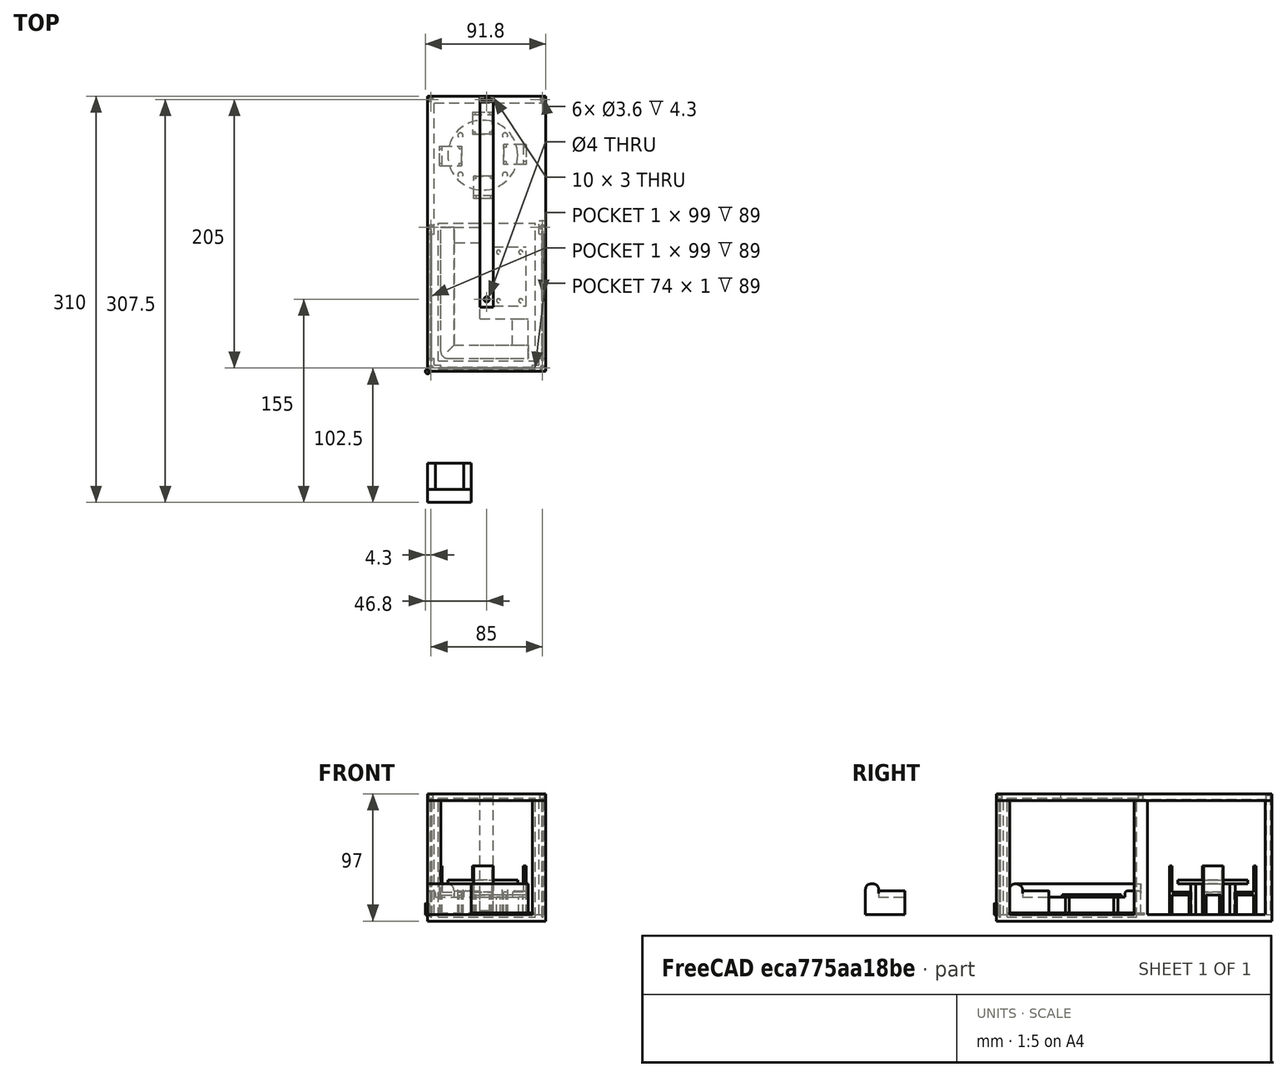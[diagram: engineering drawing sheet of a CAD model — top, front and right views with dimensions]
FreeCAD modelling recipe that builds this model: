
FCSTD DOCUMENT  (FreeCAD 0.15R4671 (Git))
Label: Salon
License: CreativeCommons Attribution-ShareAlike
LicenseURL: http://creativecommons.org/licenses/by-sa/4.0/
objects: Part::Box×28, Part::Feature×14, Part::MultiFuse×12, Part::Cut×5, Part::Cylinder×4, Part::FeaturePython×3, App::DocumentObjectGroup×2, Part::Fillet×2, Part::Offset×1
note: 69 computed .brp shape members not serialized (recipe doc carries the construction recipe); baked Part::Feature solids carry a one-line shape summary decoded from their .brp

FEATURE [Part::Box] Box  label="suelo macizo conteiner 20""
  Height = 5
  Length = 90
  Placement = pos=(0,0,-5) rot=(0,0,1;0rad)
  Width = 210
FEATURE [Part::Box] Box001  label="Techo macizo conteiner 20""
  Height = 5
  Length = 90
  Placement = pos=(0,0,87) rot=(0,0,1;0rad)
  Width = 210
FEATURE [Part::Box] Box002  label="larguero vertical esquina 1_1"
  Height = 87
  Length = 10
  Width = 5
FEATURE [Part::Box] Box003  label="larguero vertical esquina 1_2"
  Height = 87
  Length = 5
  Width = 10
FEATURE [Part::MultiFuse] Fusion  label="Larguero esquina 1 Salon"
  Shapes = -> [Box002,Box003]
FEATURE [Part::Box] Box004  label="larguero vertical esquina 2_1"
  Height = 87
  Length = 10
  Placement = pos=(80,0,0) rot=(0,0,1;0rad)
  Width = 5
FEATURE [Part::Box] Box005  label="larguero vertical esquina 2_2"
  Height = 87
  Length = 5
  Placement = pos=(85,0,0) rot=(0,0,1;0rad)
  Width = 10
FEATURE [Part::MultiFuse] Fusion001  label="Larguero esquina 2 Salon"
  Shapes = -> [Box004,Box005]
FEATURE [Part::Box] Box007  label="Tabique macizo trasero salon"
  Height = 87
  Length = 5
  Placement = pos=(85,205,0) rot=(0,0,1;0rad)
  Width = 5
FEATURE [Part::Box] Box008  label="Tabique macizo lateral salon"
  Height = 87
  Length = 80
  Placement = pos=(5,205,0) rot=(0,0,1;0rad)
  Width = 5
FEATURE [Part::Box] Box009  label="Esquina maciza linde derecha con modulo entrada"
  Height = 87
  Length = 5
  Placement = pos=(0,105,0) rot=(0,0,1;0rad)
  Width = 105
FEATURE [Part::MultiFuse] Fusion002  label="Pared Esquinazo Salon"
  Shapes = -> [Box007,Box008,Box009]
FEATURE [Part::Cylinder] Cylinder002  label="conector master"
  Angle = 360
  Height = 8
  Radius = 1.5
FEATURE [Part::Offset] Offset  label="Offset conector master"
  Fill = false
  Intersection = false
  Join = 2
  Mode = 1
  SelfIntersection = false
  Source = -> Cylinder002
  Value = 0.3
FEATURE [Part::Feature] Offset001001  label="Vaciado conector 1"
  Placement = pos=(2.5,2.5,83) rot=(0,0,1;0rad)
  shape: bbox 3.602 x 3.602 x 8.602 mm, 3 faces (baked)
FEATURE [Part::Feature] Offset002001  label="Vaciado conector 2"
  Placement = pos=(87.5,2.5,83) rot=(0,0,1;0rad)
  shape: bbox 3.602 x 3.602 x 8.602 mm, 3 faces (baked)
FEATURE [Part::Feature] Offset002002002001  label="Vaciado conector 3"
  Placement = pos=(87.5,110,83) rot=(0,0,1;0rad)
  shape: bbox 3.602 x 3.602 x 8.602 mm, 3 faces (baked)
FEATURE [Part::Feature] Offset002002002002001  label="Vaciado conector 4"
  Placement = pos=(87.5,207.5,83) rot=(0,0,1;0rad)
  shape: bbox 3.602 x 3.602 x 8.602 mm, 3 faces (baked)
FEATURE [Part::Feature] Offset001002  label="Vaciado conector 5"
  Placement = pos=(2.5,207.5,83) rot=(0,0,1;0rad)
  shape: bbox 3.602 x 3.602 x 8.602 mm, 3 faces (baked)
FEATURE [Part::Feature] Offset001002002001  label="Vaciado conector 6"
  Placement = pos=(2.5,110,83) rot=(0,0,1;0rad)
  shape: bbox 3.602 x 3.602 x 8.602 mm, 3 faces (baked)
FEATURE [Part::Box] Box020  label="cristal salon lateral"
  Height = 91
  Length = 74
  Placement = pos=(8,2,-2) rot=(0,0,1;0rad)
  Width = 1
FEATURE [Part::Box] Box021002  label="cristal salon trasero"
  Height = 91
  Length = 1
  Placement = pos=(2,8,-2) rot=(0,0,1;0rad)
  Width = 99
FEATURE [Part::Feature] Cylinder003001  label="Hueco Techo Led Salon"
  Placement = pos=(45,55,81) rot=(0,0,1;0rad)
  shape: bbox 4 x 4 x 10 mm, 3 faces (baked)
FEATURE [Part::Box] Box021003006  label="Cristal salon frontal"
  Height = 91
  Length = 1
  Placement = pos=(87,8,-2) rot=(0,0,1;0rad)
  Width = 99
FEATURE [Part::Box] Box021003007  label="Tabique izquierdo union con modulo entrada "
  Height = 87
  Length = 5
  Placement = pos=(85,105,0) rot=(0,0,1;0rad)
  Width = 10
FEATURE [Part::Feature] Cylinder002001  label="conector 1"
  Placement = pos=(2.5,2.5,83) rot=(0,0,1;0rad)
  shape: bbox 3 x 3 x 8 mm, 3 faces (baked)
FEATURE [Part::Feature] Cylinder002001001  label="conector 2"
  Placement = pos=(87.5,2.5,83) rot=(0,0,1;0rad)
  shape: bbox 3 x 3 x 8 mm, 3 faces (baked)
FEATURE [Part::Feature] Cylinder002001002  label="conector 3"
  Placement = pos=(87.5,110,83) rot=(0,0,1;0rad)
  shape: bbox 3 x 3 x 8 mm, 3 faces (baked)
FEATURE [Part::Feature] Cylinder002001003  label="conector 4"
  Placement = pos=(87.5,207.5,83) rot=(0,0,1;0rad)
  shape: bbox 3 x 3 x 8 mm, 3 faces (baked)
FEATURE [Part::Feature] Cylinder002001004  label="conector 5"
  Placement = pos=(2.5,207.5,83) rot=(0,0,1;0rad)
  shape: bbox 3 x 3 x 8 mm, 3 faces (baked)
FEATURE [Part::Feature] Cylinder002001005  label="conector 6"
  Placement = pos=(2.5,110,83) rot=(0,0,1;0rad)
  shape: bbox 3 x 3 x 8 mm, 3 faces (baked)
FEATURE [Part::MultiFuse] Fusion003  label="Union conectores"
  Shapes = -> [Cylinder002001,Cylinder002001001,Cylinder002001002,Cylinder002001003,Cylinder002001004,Cylinder002001005]
FEATURE [Part::MultiFuse] Fusion004  label="Union vaciados"
  Shapes = -> [Offset001001,Offset002001,Offset002002002001,Offset002002002002001,Offset001002,Offset001002002001]
FEATURE [Part::MultiFuse] Fusion005  label="Union suelo +paredes+conectores Salon"
  Shapes = -> [Box,Fusion,Fusion001,Box021003007,Fusion002,Fusion003]
FEATURE [Part::MultiFuse] Fusion006  label="Union cristales salon"
  Shapes = -> [Box020,Box021002,Box021003006]
FEATURE [Part::Cut] Cut  label="Suelo+Paredes Salon"
  Base = -> Fusion005
  Tool = -> Fusion006
FEATURE [Part::Cut] Cut001  label="Techo salon - vaciados conectores"
  Base = -> Box001
  Tool = -> Fusion004
FEATURE [Part::Box] Box021003008  label="Roza techo horizontal"
  Height = 5
  Length = 10
  Placement = pos=(40,49,88) rot=(0,0,1;0rad)
  Width = 160
FEATURE [Part::Box] Box021003009  label="Roza vertical"
  Height = 93
  Length = 10
  Placement = pos=(40,206,0) rot=(0,0,1;0rad)
  Width = 3
FEATURE [Part::Box] Box021003010  label="Salida cables roza hacia caja electronica"
  Height = 3
  Length = 10
  Placement = pos=(40,206,0) rot=(0,0,1;0rad)
  Width = 10
FEATURE [Part::MultiFuse] Fusion007  label="Roza led salon"
  Shapes = -> [Cylinder003001,Box021003008,Box021003009,Box021003010]
FEATURE [Part::Cut] Cut002  label="Suelo+Paredes Salon001"
  Base = -> Cut
  Tool = -> Fusion007
FEATURE [Part::Cut] Cut003  label="Techo - roza cable led"
  Base = -> Cut001
  Tool = -> Fusion007
FEATURE [Part::Cut] Cut004  label="Techo salon"
  Base = -> Cut003
  Tool = -> Fusion006
FEATURE [App::DocumentObjectGroup] Grupo001  label="Elementos constructivos Salon"
  Group = -> [Offset,Cut002,Cut004]
FEATURE [Part::Box] Box021003011  label="alfombra salon"
  Height = 1.2
  Length = 74
  Placement = pos=(8,8,0) rot=(0,0,1;0rad)
  Width = 105
FEATURE [Part::Box] Box021003013  label="respaldo izquierda"
  Height = 23.3333
  Length = 66.6667
  Width = 10
FEATURE [Part::Box] Box021003014  label="respaldo derecha"
  Height = 23.3333
  Length = 10
  Width = 100
FEATURE [Part::Box] Box021003015  label="asiento derecha"
  Height = 13.3333
  Length = 30
  Width = 100
FEATURE [Part::Box] Box021003016  label="Asiento izquierda"
  Height = 13.3333
  Length = 66.6667
  Width = 30
FEATURE [Part::Box] Box021003017  label="reposabrazos derecho"
  Height = 18
  Length = 30
  Placement = pos=(0,88,0) rot=(0,0,1;0rad)
  Width = 12
FEATURE [Part::Box] Box021003018  label="reposabrazos izquierdo"
  Height = 18
  Length = 12
  Placement = pos=(54.6667,0,0) rot=(0,0,1;0rad)
  Width = 30
FEATURE [Part::MultiFuse] Fusion008  label="Sofa salon"
  Placement = pos=(10,10,0) rot=(0,0,1;0rad)
  Shapes = -> [Box021003013,Box021003014,Box021003015,Box021003016,Box021003017,Box021003018]
FEATURE [Part::Fillet] Fillet  label="Sofa"
  Base = -> Fusion008
  Edges = 12 edges: [Edge5 r=5,Edge8 r=2,Edge12 r=2,Edge13 r=5,Edge19 r=2,Edge21 r=2,Edge25 r=4,Edge26 r=4,Edge27 r=4,Edge28 r=4,Edge37 r=5,Edge38 r=5]
FEATURE [Part::Box] Box021003019  label="tablero mesa sofa"
  Height = 2
  Length = 25
  Placement = pos=(50,50,13.3333) rot=(0,0,1;0rad)
  Width = 45
FEATURE [Part::Cylinder] Cylinder  label="pata mesa master"
  Angle = 360
  Height = 13.3333
  Placement = pos=(54,54,0) rot=(0,0,1;0rad)
  Radius = 1.5
FEATURE [Part::FeaturePython] Array  label="matriz 4 patas mesa sofa"  # Draft array (typed FeaturePython)
  Angle = 360
  ArrayType = 0
  Axis = (0,0,1)
  Base = -> Cylinder
  Center = (0,0,0)
  Fuse = false
  IntervalAxis = (0,0,0)
  IntervalX = (17,0,0)
  IntervalY = (0,37,0)
  IntervalZ = (0,0,0)
  NumberPolar = 1
  NumberX = 2
  NumberY = 2
  NumberZ = 1
FEATURE [Part::MultiFuse] Fusion009  label="mesa sofa"
  Shapes = -> [Box021003019,Array]
FEATURE [Part::Cylinder] Cylinder002001006  label="tablero mesa comedor"
  Angle = 360
  Height = 3
  Placement = pos=(42,165,23.3333) rot=(0,0,1;0rad)
  Radius = 26.6667
FEATURE [Part::Cylinder] Cylinder002001007  label="pata master mesa comedor"
  Angle = 360
  Height = 23.3333
  Placement = pos=(25,150,0) rot=(0,0,1;0rad)
  Radius = 2
FEATURE [Part::FeaturePython] Array001  label="matriz 4 patas mesa comedor"  # Draft array (typed FeaturePython)
  Angle = 360
  ArrayType = 0
  Axis = (0,0,1)
  Base = -> Cylinder002001007
  Center = (0,0,0)
  Fuse = false
  IntervalAxis = (0,0,0)
  IntervalX = (34,0,0)
  IntervalY = (0,30,0)
  IntervalZ = (0,0,0)
  NumberPolar = 1
  NumberX = 2
  NumberY = 2
  NumberZ = 1
FEATURE [Part::MultiFuse] Fusion010  label="mesa comedor"
  Shapes = -> [Cylinder002001006,Array001]
FEATURE [Part::Feature] Fusion011  label="Silla master"
  Placement = pos=(50,132,0) rot=(0,0,1;1.5708rad)
  shape: bbox 15 x 17 x 37 mm, 20 faces (baked)
FEATURE [Part::FeaturePython] Array002  label="Conjunto 4 sillas comedor"  # Draft array (typed FeaturePython)
  Angle = 360
  ArrayType = 1
  Axis = (0,0,1)
  Base = -> Fusion011
  Center = (42,165,0)
  Fuse = false
  IntervalAxis = (0,0,0)
  IntervalX = (1,0,0)
  IntervalY = (0,1,0)
  IntervalZ = (0,0,0)
  NumberPolar = 4
  NumberX = 2
  NumberY = 2
  NumberZ = 1
FEATURE [Part::Box] Box021003020  label="respaldo"
  Height = 23.3333
  Length = 33.3333
  Width = 10
FEATURE [Part::Box] Box021003023  label="Asiento"
  Height = 13.3333
  Length = 33.3333
  Width = 30
FEATURE [Part::Box] Box021003025  label="reposabrazos izquierdo butaca porche"
  Height = 18
  Length = 6
  Placement = pos=(27.3333,0,0) rot=(0,0,1;0rad)
  Width = 30
FEATURE [Part::Box] Box021003026  label="reposabrazos derecho butaca porche"
  Height = 18
  Length = 6
  Width = 30
FEATURE [Part::MultiFuse] Fusion012  label="Butaca porche sin redondeos"
  Shapes = -> [Box021003020,Box021003023,Box021003025,Box021003026]
FEATURE [Part::Fillet] Fillet001  label="Butaca porche"
  Base = -> Fusion012
  Edges = 6 edges: [Edge2 r=4,Edge4 r=4,Edge12 r=2,Edge14 r=2,Edge19 r=2,Edge22 r=2]
  Placement = pos=(0,-100,0) rot=(0,0,1;0rad)
FEATURE [App::DocumentObjectGroup] Grupo  label="muebles salon"
  Group = -> [Box021003011,Fillet,Fusion009,Fusion010,Array002,Fillet001]
